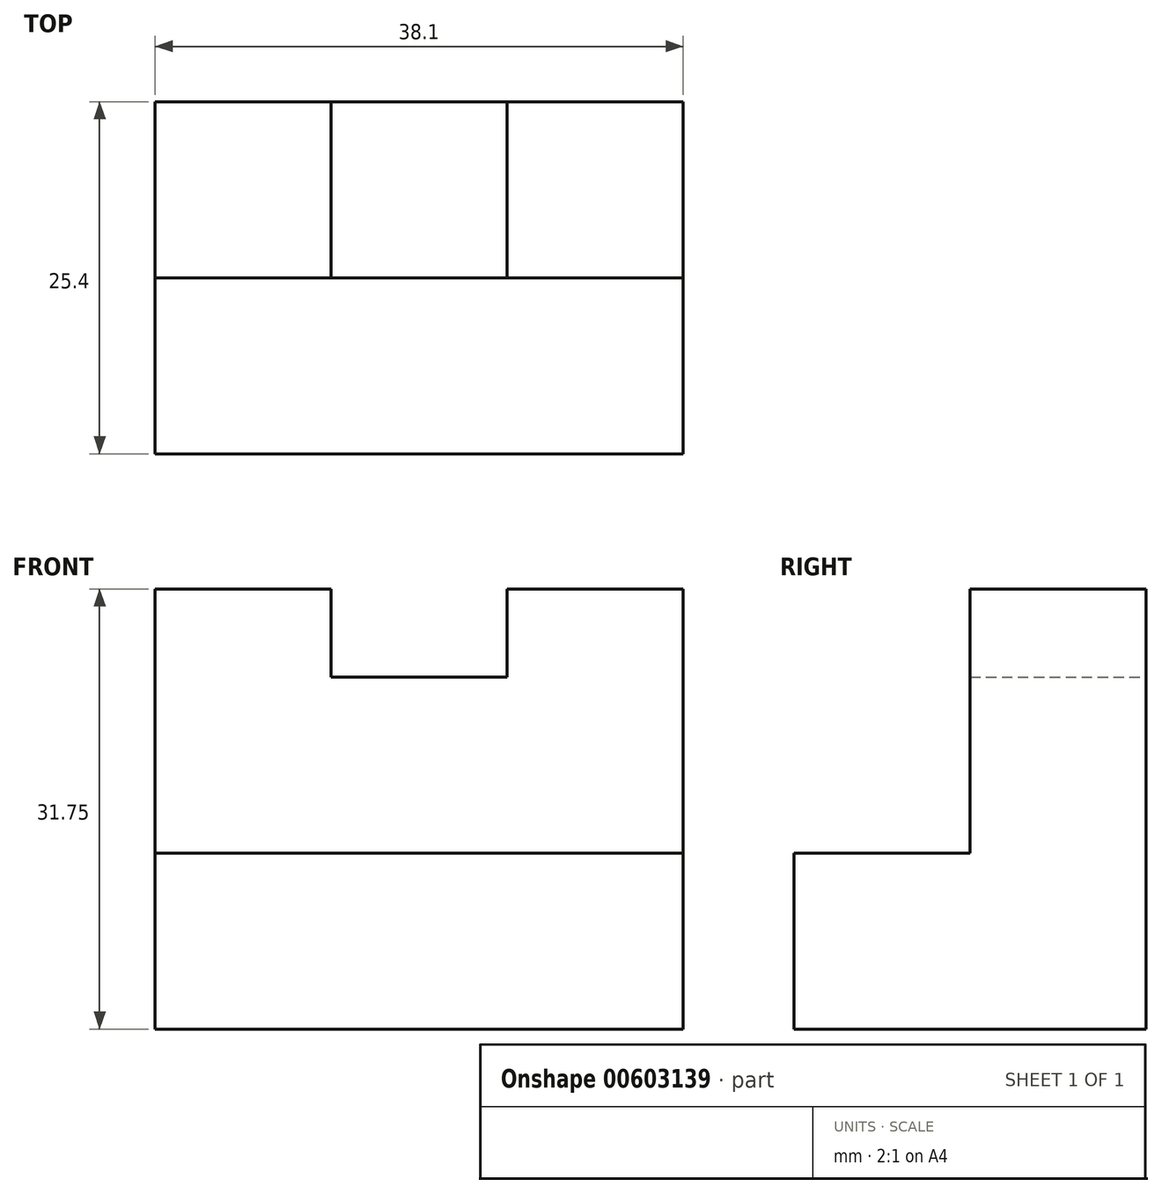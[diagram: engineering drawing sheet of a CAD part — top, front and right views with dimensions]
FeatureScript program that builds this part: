
annotation { "Feature Type Name" : "Feature", "Feature Type Description" : "" }
export const myFeature = defineFeature(function(context is Context, id is Id, definition is map)
    precondition{}
    {
        {
            var Q0;
            Q0=qCreatedBy(makeId("Right.planeOp"),FACE);
            var sketch = newSketch(context, id + "F0", { "sketchPlane" : qUnion([Q0])});
            skLineSegment(sketch, "E0", {"start": v(0, 0) * mm, "end": v(0, 31.75) * mm});
            skLineSegment(sketch, "E1", {"start": v(0, 31.75) * mm, "end": v(-12.7, 31.75) * mm});
            skLineSegment(sketch, "E2", {"start": v(-12.7, 31.75) * mm, "end": v(-12.7, 12.7) * mm});
            skLineSegment(sketch, "E3", {"start": v(-12.7, 12.7) * mm, "end": v(-25.4, 12.7) * mm});
            skLineSegment(sketch, "E4", {"start": v(-25.4, 12.7) * mm, "end": v(-25.4, 0) * mm});
            skLineSegment(sketch, "E5", {"start": v(-25.4, 0) * mm, "end": v(0, 0) * mm});
            skSolve(sketch);
        }
        {
            var Q0;
            Q0 = qSketchRegion(id + "F0", true);
            extrude(context, id + "F1", {"entities" : qUnion([Q0]), "depth" : 38.1 * mm, "offsetDistance" : 25.4 * mm});
        }
        {
            var Q0;
            Q0=makeQuery(id+"F1.opExtrude","SWEPT_FACE",FACE,{"disambiguationData":[OSD([sQuery(id+"F0.wireOp",EDGE,"E1")])]});
            var sketch = newSketch(context, id + "F2", { "sketchPlane" : qUnion([Q0])});
            skLineSegment(sketch, "E6", {"start": v(12.7, -12.7) * mm, "end": v(12.7, 0) * mm});
            skLineSegment(sketch, "E7", {"start": v(12.7, -12.7) * mm, "end": v(25.4, -12.7) * mm});
            skLineSegment(sketch, "E8", {"start": v(25.4, -12.7) * mm, "end": v(25.4, 0) * mm});
            skLineSegment(sketch, "E9", {"start": v(25.4, 0) * mm, "end": v(12.7, 0) * mm});
            skSolve(sketch);
        }
        {
            var Q0;
            Q0=makeQuery(id+"F2.imprint","IMPRINT",FACE,{"disambiguationData":[TD([[makeQuery(id+"F2.imprint","IMPRINT",EDGE,{"derivedFrom":sQuery(id+"F2.wireOp",EDGE,"E6")}),-1.0]])]});
            extrude(context, id + "F3", {"entities" : qUnion([Q0]), "operationType" : NewBodyOperationType.REMOVE, "oppositeDirection" : true, "depth" : 6.35 * mm, "offsetDistance" : 25.4 * mm});
        }
    });
